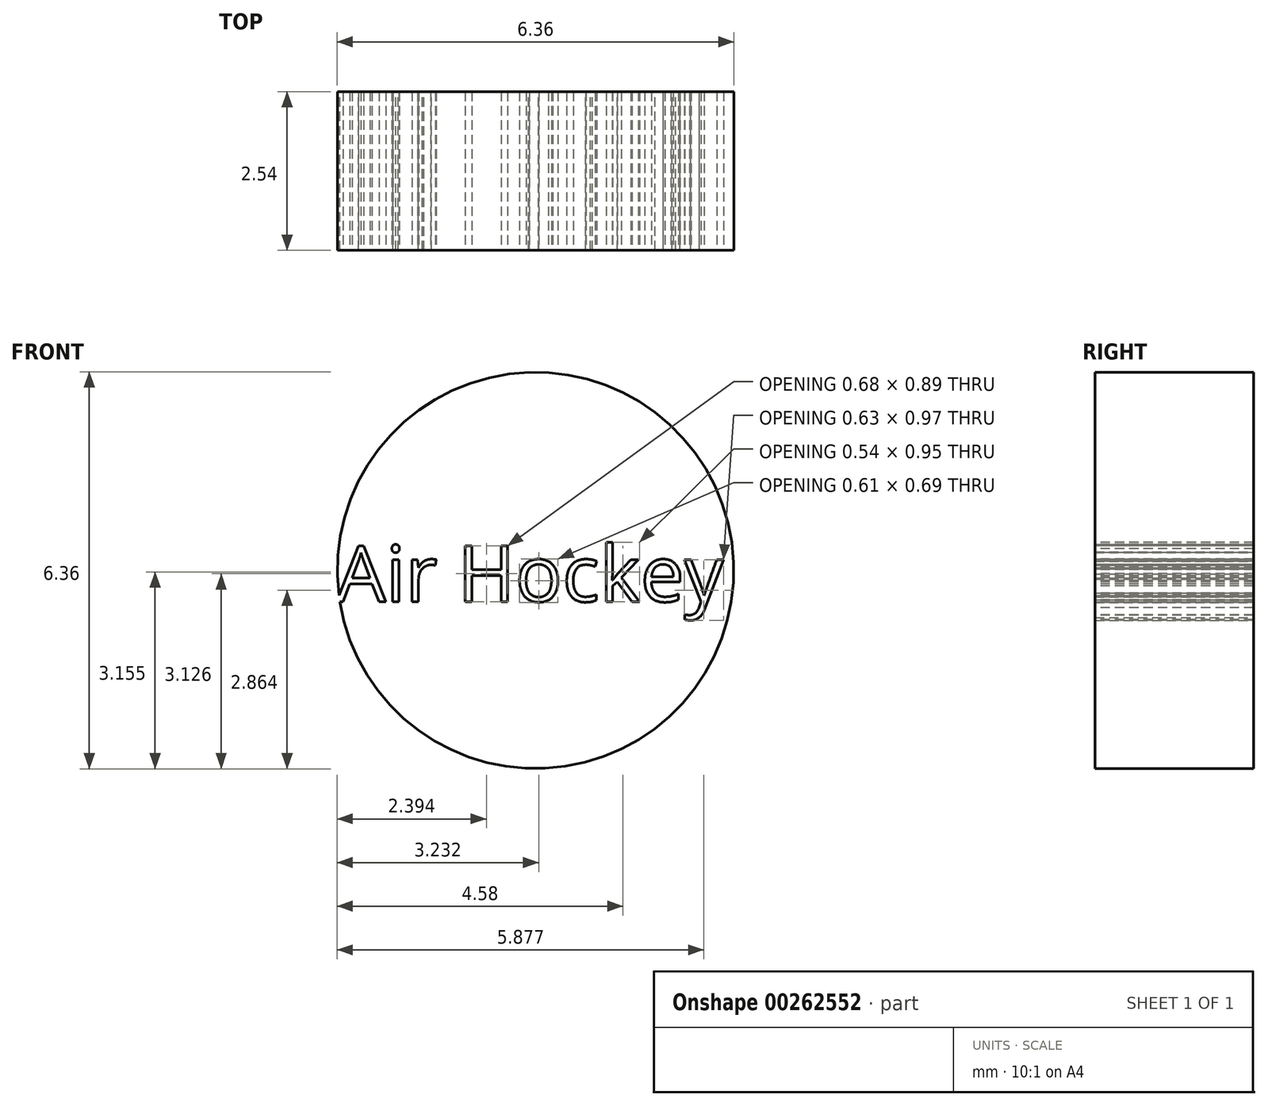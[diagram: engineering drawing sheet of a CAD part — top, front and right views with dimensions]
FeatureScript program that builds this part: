
annotation { "Feature Type Name" : "Feature", "Feature Type Description" : "" }
export const myFeature = defineFeature(function(context is Context, id is Id, definition is map)
    precondition{}
    {
        {
            var Q0;
            Q0=qCreatedBy(makeId("Front.planeOp"),FACE);
            var sketch = newSketch(context, id + "F0", { "sketchPlane" : qUnion([Q0])});
            skCircle(sketch, "E0", {"center": v(0, 0) * mm, "radius": 3.18 * mm});
            skSolve(sketch);
        }
        {
            var Q0;
            Q0=makeQuery(id+"F0.imprint","IMPRINT",FACE,{"disambiguationData":[TD([[makeQuery(id+"F0.imprint","IMPRINT",EDGE,{"derivedFrom":sQuery(id+"F0.wireOp",EDGE,"E0")}),1.0]])]});
            extrude(context, id + "F1", {"entities" : qUnion([Q0]), "depth" : 2.54 * mm});
        }
        {
            var Q0;
            Q0=makeQuery(id+"F1.opExtrude","CAP_FACE",FACE,{"disambiguationData":[OSD([sQuery(id+"F0.wireOp",EDGE,"E0")])],"isStart":false});
            var sketch = newSketch(context, id + "F2", { "sketchPlane" : qUnion([Q0])});
            skText(sketch, "E1", { "text": "Air Hockey\n", "fontName": "OpenSans-Regular.ttf"});
            const initialGuessF2  = {"E1": [-0.00319, -0.0005, 1, 0, 0.0009]};
            skSetInitialGuess(sketch, initialGuessF2);
            skSolve(sketch);
        }
        {
            var Q0;
            Q0 = qSketchRegion(id + "F2", true);
            extrude(context, id + "F3", {"entities" : qUnion([Q0]), "operationType" : NewBodyOperationType.REMOVE, "endBound" : BoundingType.THROUGH_ALL, "oppositeDirection" : true, "depth" : 0.25 * mm});
        }
    });
